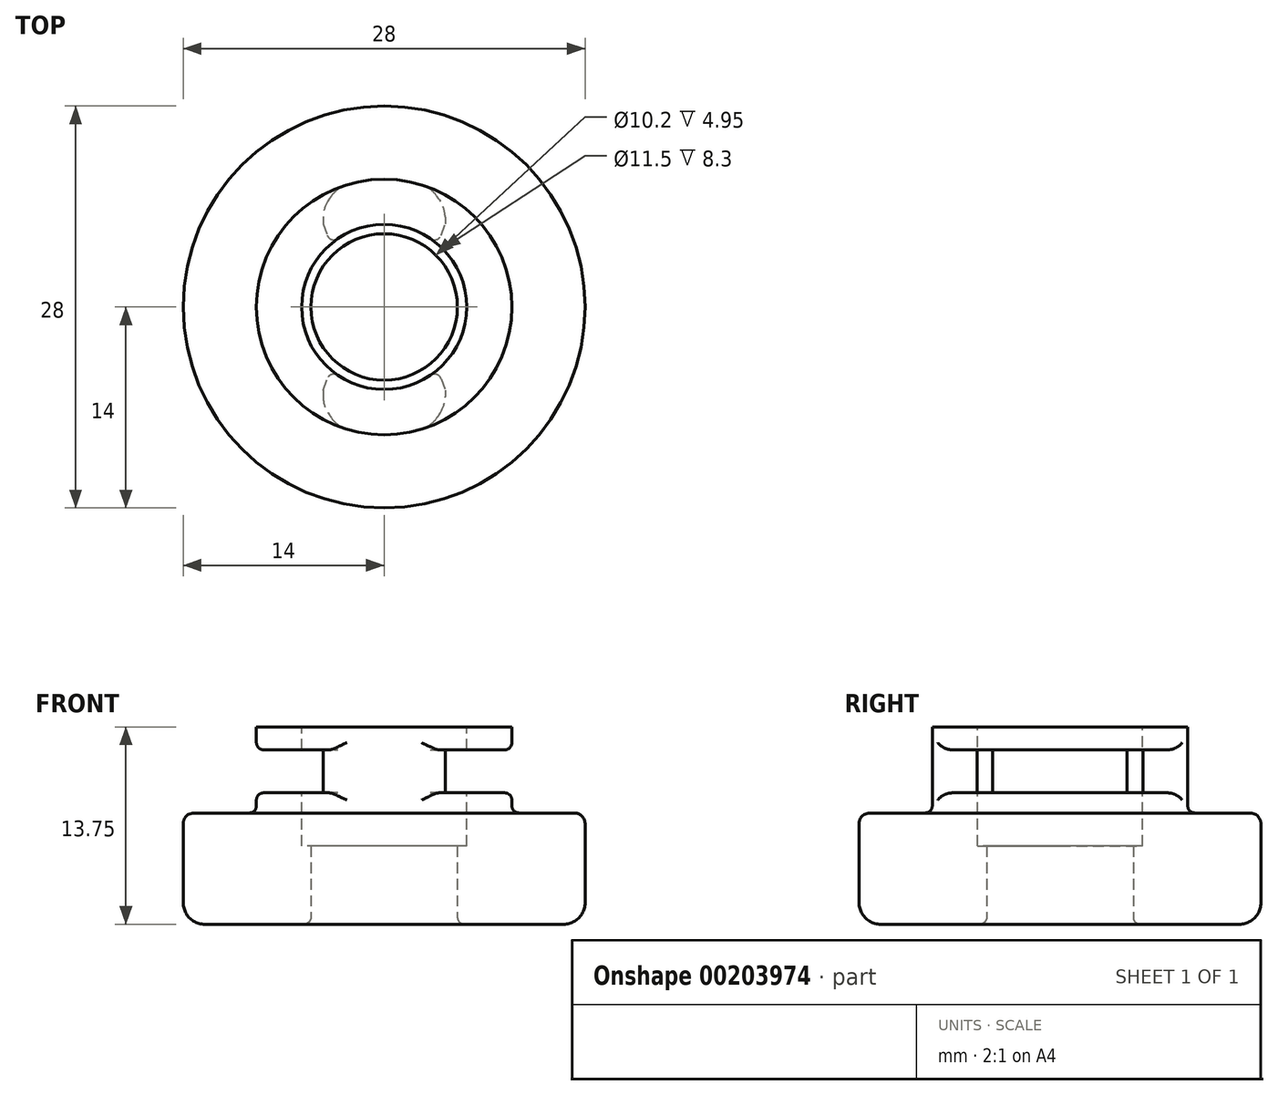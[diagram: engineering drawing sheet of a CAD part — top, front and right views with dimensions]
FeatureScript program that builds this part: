
annotation { "Feature Type Name" : "Feature", "Feature Type Description" : "" }
export const myFeature = defineFeature(function(context is Context, id is Id, definition is map)
    precondition{}
    {
        {
            var Q0;
            Q0=qCreatedBy(makeId("Top.planeOp"),FACE);
            var sketch = newSketch(context, id + "F0", { "sketchPlane" : qUnion([Q0])});
            skCircle(sketch, "E0", {"center": v(0, 0) * mm, "radius": 14 * mm});
            skCircle(sketch, "E1", {"center": v(0, 0) * mm, "radius": 5.1 * mm});
            skSolve(sketch);
        }
        {
            var Q0;
            Q0=makeQuery(id+"F0.imprint","IMPRINT",FACE,{"disambiguationData":[TD([[makeQuery(id+"F0.imprint","IMPRINT",EDGE,{"derivedFrom":sQuery(id+"F0.wireOp",EDGE,"E0")}),1.0]])]});
            extrude(context, id + "F1", {"entities" : qUnion([Q0]), "depth" : 13.75 * mm});
        }
        {
            var Q0;
            Q0=makeQuery(id+"F1.opExtrude","CAP_FACE",FACE,{"disambiguationData":[OSD([sQuery(id+"F0.wireOp",EDGE,"E0"),sQuery(id+"F0.wireOp",EDGE,"E1")])],"isStart":false});
            var sketch = newSketch(context, id + "F2", { "sketchPlane" : qUnion([Q0])});
            skCircle(sketch, "E2", {"center": v(0, 0) * mm, "radius": 8.9 * mm});
            skCircle(sketch, "E3", {"center": v(0, 0) * mm, "radius": 21.17 * mm});
            skSolve(sketch);
        }
        {
            var Q0;
            Q0=makeQuery(id+"F2.imprint","IMPRINT",FACE,{"disambiguationData":[TD([[makeQuery(id+"F2.imprint","IMPRINT",EDGE,{"derivedFrom":sQuery(id+"F2.wireOp",EDGE,"E3")}),1.0]])]});
            var Q1;
            Q1=makeQuery(id+"F2.imprint","IMPRINT",FACE,{"disambiguationData":[TD([[makeQuery(id+"F2.imprint","IMPRINT",EDGE,{"derivedFrom":sQuery(id+"F2.wireOp",EDGE,"E2")}),-1.0]])]});
            extrude(context, id + "F3", {"entities" : qUnion([Q0, Q1]), "operationType" : NewBodyOperationType.REMOVE, "oppositeDirection" : true, "depth" : 6 * mm});
        }
        {
            var Q0;
            Q0=qCreatedBy(makeId("Front.planeOp"),FACE);
            var sketch = newSketch(context, id + "F4", { "sketchPlane" : qUnion([Q0])});
            skLineSegment(sketch, "E4.bottom", {"start": v(-30.77, 12.15) * mm, "end": v(-4.25, 12.15) * mm});
            skLineSegment(sketch, "E4.top", {"start": v(-30.77, 9.15) * mm, "end": v(-4.25, 9.15) * mm});
            skLineSegment(sketch, "E4.left", {"start": v(-30.77, 12.15) * mm, "end": v(-30.77, 9.15) * mm});
            skLineSegment(sketch, "E4.right", {"start": v(-4.25, 12.15) * mm, "end": v(-4.25, 9.15) * mm});
            skLineSegment(sketch, "E5.bottom", {"start": v(4.25, 12.15) * mm, "end": v(38.35, 12.15) * mm});
            skLineSegment(sketch, "E5.top", {"start": v(4.25, 9.15) * mm, "end": v(38.35, 9.15) * mm});
            skLineSegment(sketch, "E5.left", {"start": v(4.25, 12.15) * mm, "end": v(4.25, 9.15) * mm});
            skLineSegment(sketch, "E5.right", {"start": v(38.35, 12.15) * mm, "end": v(38.35, 9.15) * mm});
            skSolve(sketch);
        }
        {
            var Q0;
            Q0=makeQuery(id+"F4.imprint","IMPRINT",FACE,{"disambiguationData":[TD([[makeQuery(id+"F4.imprint","IMPRINT",EDGE,{"derivedFrom":sQuery(id+"F4.wireOp",EDGE,"E4.bottom")}),-1.0]])]});
            var Q1;
            Q1=makeQuery(id+"F4.imprint","IMPRINT",FACE,{"disambiguationData":[TD([[makeQuery(id+"F4.imprint","IMPRINT",EDGE,{"derivedFrom":sQuery(id+"F4.wireOp",EDGE,"E5.bottom")}),-1.0]])]});
            extrude(context, id + "F5", {"entities" : qUnion([Q0, Q1]), "operationType" : NewBodyOperationType.REMOVE, "endBound" : BoundingType.SYMMETRIC, "oppositeDirection" : true, "depth" : 25 * mm});
        }
        {
            var Q0;
            Q0=makeQuery(id+"F1.opExtrude","CAP_FACE",FACE,{"disambiguationData":[OSD([sQuery(id+"F0.wireOp",EDGE,"E0"),sQuery(id+"F0.wireOp",EDGE,"E1")])],"isStart":false});
            var sketch = newSketch(context, id + "F6", { "sketchPlane" : qUnion([Q0])});
            skCircle(sketch, "E6", {"center": v(0, 0) * mm, "radius": 5.75 * mm});
            skSolve(sketch);
        }
        {
            var Q0;
            Q0=makeQuery(id+"F6.imprint","IMPRINT",FACE,{"disambiguationData":[TD([[makeQuery(id+"F6.imprint","IMPRINT",EDGE,{"derivedFrom":sQuery(id+"F6.wireOp",EDGE,"E6")}),1.0]])]});
            var Q1;
            Q1=makeQuery(id+"F6.imprint","IMPRINT",FACE,{"disambiguationData":[TD([[makeQuery(id+"F6.imprint","IMPRINT",EDGE,{"derivedFrom":makeQuery(id+"F1.opExtrude","CAP_EDGE",EDGE,{"disambiguationData":[OSD([sQuery(id+"F0.wireOp",EDGE,"E1")])],"isStart":false})}),1.0]])]});
            extrude(context, id + "F7", {"entities" : qUnion([Q0, Q1]), "operationType" : NewBodyOperationType.REMOVE, "oppositeDirection" : true, "depth" : 8.3 * mm});
        }
        {
            var Q0;
            Q0=makeQuery(id+"F1.opExtrude","CAP_EDGE",EDGE,{"disambiguationData":[OSD([sQuery(id+"F0.wireOp",EDGE,"E1")])],"isStart":true});
            fillet(context, id + "F8", {"entities" : qUnion([Q0]), "radius" : 0.5 * mm, "tangentPropagation" : true, "allowEdgeOverflow" : false});
        }
        {
            var Q0;
            Q0=makeQuery(id+"F1.opExtrude","CAP_EDGE",EDGE,{"disambiguationData":[OSD([sQuery(id+"F0.wireOp",EDGE,"E0")])],"isStart":true});
            fillet(context, id + "F9", {"entities" : qUnion([Q0]), "radius" : 1.5 * mm, "tangentPropagation" : true, "allowEdgeOverflow" : false});
        }
        {
            var Q0;
            Q0=makeQuery(id+"F3.boolean.opBoolean","INTERSECT",EDGE,{"derivedFrom":[makeQuery(id+"F1.opExtrude","SWEPT_FACE",FACE,{"disambiguationData":[OSD([sQuery(id+"F0.wireOp",EDGE,"E0")])]}),makeQuery(id+"F3.opExtrude","CAP_FACE",FACE,{"disambiguationData":[OSD([sQuery(id+"F2.wireOp",EDGE,"E2"),sQuery(id+"F2.wireOp",EDGE,"E3")])],"isStart":false})]});
            fillet(context, id + "F10", {"entities" : qUnion([Q0]), "radius" : 0.75 * mm, "tangentPropagation" : true, "allowEdgeOverflow" : false});
        }
        {
            var Q0;
            Q0=makeQuery(id+"F3.boolean.opBoolean","COPY",EDGE,{"derivedFrom":makeQuery(id+"F3.opExtrude","CAP_EDGE",EDGE,{"disambiguationData":[OSD([sQuery(id+"F2.wireOp",EDGE,"E2")])],"isStart":false})});
            var Q1;
            Q1=makeQuery(id+"F3.boolean.opBoolean","COPY",EDGE,{"derivedFrom":makeQuery(id+"F3.opExtrude","CAP_EDGE",EDGE,{"disambiguationData":[OSD([sQuery(id+"F2.wireOp",EDGE,"E2")])],"isStart":true})});
            var Q2;
            Q2=makeQuery(id+"F7.boolean.opBoolean","COPY",EDGE,{"derivedFrom":makeQuery(id+"F7.opExtrude","CAP_EDGE",EDGE,{"disambiguationData":[OSD([sQuery(id+"F6.wireOp",EDGE,"E6")])],"isStart":true})});
            fillet(context, id + "F11", {"entities" : qUnion([Q0, Q1, Q2]), "radius" : 0.5 * mm, "tangentPropagation" : true, "allowEdgeOverflow" : false});
        }
        {
            var Q0;
            Q0=makeQuery(id+"F5.boolean.opBoolean","INTERSECT",EDGE,{"disambiguationData":[OD(1.0)],"derivedFrom":[makeQuery(id+"F3.boolean.opBoolean","COPY",FACE,{"derivedFrom":makeQuery(id+"F3.opExtrude","SWEPT_FACE",FACE,{"disambiguationData":[OSD([sQuery(id+"F2.wireOp",EDGE,"E2")])]})}),makeQuery(id+"F5.opExtrude","SWEPT_FACE",FACE,{"disambiguationData":[OSD([sQuery(id+"F4.wireOp",EDGE,"E4.right")])]})]});
            var Q1;
            Q1=makeQuery(id+"F5.boolean.opBoolean","INTERSECT",EDGE,{"disambiguationData":[OD(0.0)],"derivedFrom":[makeQuery(id+"F3.boolean.opBoolean","COPY",FACE,{"derivedFrom":makeQuery(id+"F3.opExtrude","SWEPT_FACE",FACE,{"disambiguationData":[OSD([sQuery(id+"F2.wireOp",EDGE,"E2")])]})}),makeQuery(id+"F5.opExtrude","SWEPT_FACE",FACE,{"disambiguationData":[OSD([sQuery(id+"F4.wireOp",EDGE,"E4.right")])]})]});
            var Q2;
            Q2=makeQuery(id+"F5.boolean.opBoolean","INTERSECT",EDGE,{"disambiguationData":[OD(0.0)],"derivedFrom":[makeQuery(id+"F3.boolean.opBoolean","COPY",FACE,{"derivedFrom":makeQuery(id+"F3.opExtrude","SWEPT_FACE",FACE,{"disambiguationData":[OSD([sQuery(id+"F2.wireOp",EDGE,"E2")])]})}),makeQuery(id+"F5.opExtrude","SWEPT_FACE",FACE,{"disambiguationData":[OSD([sQuery(id+"F4.wireOp",EDGE,"E5.left")])]})]});
            var Q3;
            Q3=makeQuery(id+"F5.boolean.opBoolean","INTERSECT",EDGE,{"disambiguationData":[OD(1.0)],"derivedFrom":[makeQuery(id+"F3.boolean.opBoolean","COPY",FACE,{"derivedFrom":makeQuery(id+"F3.opExtrude","SWEPT_FACE",FACE,{"disambiguationData":[OSD([sQuery(id+"F2.wireOp",EDGE,"E2")])]})}),makeQuery(id+"F5.opExtrude","SWEPT_FACE",FACE,{"disambiguationData":[OSD([sQuery(id+"F4.wireOp",EDGE,"E5.left")])]})]});
            chamfer(context, id + "F12", {"entities" : qUnion([Q0, Q1, Q2, Q3]), "width" : 1.5 * mm, "tangentPropagation" : true});
        }
        {
            var Q0;
            {var subQ0=makeQuery(id+"F5.opExtrude","SWEPT_FACE",FACE,{"disambiguationData":[OSD([sQuery(id+"F4.wireOp",EDGE,"E4.right")])]});Q0=makeQuery(id+"F12.opChamfer","BLEND_EDGE",EDGE,{"blendedFrom":[makeQuery(id+"F5.boolean.opBoolean","INTERSECT",EDGE,{"disambiguationData":[OD(0.0)],"derivedFrom":[makeQuery(id+"F3.boolean.opBoolean","COPY",FACE,{"derivedFrom":makeQuery(id+"F3.opExtrude","SWEPT_FACE",FACE,{"disambiguationData":[OSD([sQuery(id+"F2.wireOp",EDGE,"E2")])]})}),subQ0]}),makeQuery(id+"F5.boolean.opBoolean","COPY",FACE,{"disambiguationData":[OD(0.0)],"derivedFrom":subQ0})],"blendedInto":[makeQuery(id+"F5.boolean.opBoolean","COPY",FACE,{"disambiguationData":[OD(0.0)],"derivedFrom":subQ0})]});}
            var Q1;
            {var subQ0=makeQuery(id+"F3.boolean.opBoolean","COPY",FACE,{"derivedFrom":makeQuery(id+"F3.opExtrude","SWEPT_FACE",FACE,{"disambiguationData":[OSD([sQuery(id+"F2.wireOp",EDGE,"E2")])]})});Q1=makeQuery(id+"F12.opChamfer","BLEND_EDGE",EDGE,{"blendedFrom":[makeQuery(id+"F5.boolean.opBoolean","INTERSECT",EDGE,{"disambiguationData":[OD(0.0)],"derivedFrom":[subQ0,makeQuery(id+"F5.opExtrude","SWEPT_FACE",FACE,{"disambiguationData":[OSD([sQuery(id+"F4.wireOp",EDGE,"E4.right")])]})]}),subQ0],"blendedInto":[subQ0]});}
            var Q2;
            {var subQ0=makeQuery(id+"F5.opExtrude","SWEPT_FACE",FACE,{"disambiguationData":[OSD([sQuery(id+"F4.wireOp",EDGE,"E4.right")])]});Q2=makeQuery(id+"F12.opChamfer","BLEND_EDGE",EDGE,{"blendedFrom":[makeQuery(id+"F5.boolean.opBoolean","INTERSECT",EDGE,{"disambiguationData":[OD(1.0)],"derivedFrom":[makeQuery(id+"F3.boolean.opBoolean","COPY",FACE,{"derivedFrom":makeQuery(id+"F3.opExtrude","SWEPT_FACE",FACE,{"disambiguationData":[OSD([sQuery(id+"F2.wireOp",EDGE,"E2")])]})}),subQ0]}),makeQuery(id+"F5.boolean.opBoolean","COPY",FACE,{"disambiguationData":[OD(1.0)],"derivedFrom":subQ0})],"blendedInto":[makeQuery(id+"F5.boolean.opBoolean","COPY",FACE,{"disambiguationData":[OD(1.0)],"derivedFrom":subQ0})]});}
            var Q3;
            {var subQ0=makeQuery(id+"F3.boolean.opBoolean","COPY",FACE,{"derivedFrom":makeQuery(id+"F3.opExtrude","SWEPT_FACE",FACE,{"disambiguationData":[OSD([sQuery(id+"F2.wireOp",EDGE,"E2")])]})});Q3=makeQuery(id+"F12.opChamfer","BLEND_EDGE",EDGE,{"blendedFrom":[makeQuery(id+"F5.boolean.opBoolean","INTERSECT",EDGE,{"disambiguationData":[OD(1.0)],"derivedFrom":[subQ0,makeQuery(id+"F5.opExtrude","SWEPT_FACE",FACE,{"disambiguationData":[OSD([sQuery(id+"F4.wireOp",EDGE,"E4.right")])]})]}),subQ0],"blendedInto":[subQ0]});}
            var Q4;
            {var subQ0=makeQuery(id+"F3.boolean.opBoolean","COPY",FACE,{"derivedFrom":makeQuery(id+"F3.opExtrude","SWEPT_FACE",FACE,{"disambiguationData":[OSD([sQuery(id+"F2.wireOp",EDGE,"E2")])]})});Q4=makeQuery(id+"F12.opChamfer","BLEND_EDGE",EDGE,{"blendedFrom":[makeQuery(id+"F5.boolean.opBoolean","INTERSECT",EDGE,{"disambiguationData":[OD(0.0)],"derivedFrom":[subQ0,makeQuery(id+"F5.opExtrude","SWEPT_FACE",FACE,{"disambiguationData":[OSD([sQuery(id+"F4.wireOp",EDGE,"E5.left")])]})]}),subQ0],"blendedInto":[subQ0]});}
            var Q5;
            {var subQ0=makeQuery(id+"F5.opExtrude","SWEPT_FACE",FACE,{"disambiguationData":[OSD([sQuery(id+"F4.wireOp",EDGE,"E5.left")])]});Q5=makeQuery(id+"F12.opChamfer","BLEND_EDGE",EDGE,{"blendedFrom":[makeQuery(id+"F5.boolean.opBoolean","INTERSECT",EDGE,{"disambiguationData":[OD(0.0)],"derivedFrom":[makeQuery(id+"F3.boolean.opBoolean","COPY",FACE,{"derivedFrom":makeQuery(id+"F3.opExtrude","SWEPT_FACE",FACE,{"disambiguationData":[OSD([sQuery(id+"F2.wireOp",EDGE,"E2")])]})}),subQ0]}),makeQuery(id+"F5.boolean.opBoolean","COPY",FACE,{"disambiguationData":[OD(0.0)],"derivedFrom":subQ0})],"blendedInto":[makeQuery(id+"F5.boolean.opBoolean","COPY",FACE,{"disambiguationData":[OD(0.0)],"derivedFrom":subQ0})]});}
            var Q6;
            {var subQ0=makeQuery(id+"F5.opExtrude","SWEPT_FACE",FACE,{"disambiguationData":[OSD([sQuery(id+"F4.wireOp",EDGE,"E5.left")])]});Q6=makeQuery(id+"F12.opChamfer","BLEND_EDGE",EDGE,{"blendedFrom":[makeQuery(id+"F5.boolean.opBoolean","INTERSECT",EDGE,{"disambiguationData":[OD(1.0)],"derivedFrom":[makeQuery(id+"F3.boolean.opBoolean","COPY",FACE,{"derivedFrom":makeQuery(id+"F3.opExtrude","SWEPT_FACE",FACE,{"disambiguationData":[OSD([sQuery(id+"F2.wireOp",EDGE,"E2")])]})}),subQ0]}),makeQuery(id+"F5.boolean.opBoolean","COPY",FACE,{"disambiguationData":[OD(1.0)],"derivedFrom":subQ0})],"blendedInto":[makeQuery(id+"F5.boolean.opBoolean","COPY",FACE,{"disambiguationData":[OD(1.0)],"derivedFrom":subQ0})]});}
            var Q7;
            {var subQ0=makeQuery(id+"F3.boolean.opBoolean","COPY",FACE,{"derivedFrom":makeQuery(id+"F3.opExtrude","SWEPT_FACE",FACE,{"disambiguationData":[OSD([sQuery(id+"F2.wireOp",EDGE,"E2")])]})});Q7=makeQuery(id+"F12.opChamfer","BLEND_EDGE",EDGE,{"blendedFrom":[makeQuery(id+"F5.boolean.opBoolean","INTERSECT",EDGE,{"disambiguationData":[OD(1.0)],"derivedFrom":[subQ0,makeQuery(id+"F5.opExtrude","SWEPT_FACE",FACE,{"disambiguationData":[OSD([sQuery(id+"F4.wireOp",EDGE,"E5.left")])]})]}),subQ0],"blendedInto":[subQ0]});}
            fillet(context, id + "F13", {"entities" : qUnion([Q0, Q1, Q2, Q3, Q4, Q5, Q6, Q7]), "radius" : 2 * mm, "tangentPropagation" : true, "allowEdgeOverflow" : false});
        }
        {
            var Q0;
            Q0=makeQuery(id+"F5.boolean.opBoolean","INTERSECT",EDGE,{"derivedFrom":[makeQuery(id+"F3.boolean.opBoolean","COPY",FACE,{"derivedFrom":makeQuery(id+"F3.opExtrude","SWEPT_FACE",FACE,{"disambiguationData":[OSD([sQuery(id+"F2.wireOp",EDGE,"E2")])]})}),makeQuery(id+"F5.opExtrude","SWEPT_FACE",FACE,{"disambiguationData":[OSD([sQuery(id+"F4.wireOp",EDGE,"E5.top")])]})]});
            var Q1;
            Q1=makeQuery(id+"F5.boolean.opBoolean","INTERSECT",EDGE,{"derivedFrom":[makeQuery(id+"F3.boolean.opBoolean","COPY",FACE,{"derivedFrom":makeQuery(id+"F3.opExtrude","SWEPT_FACE",FACE,{"disambiguationData":[OSD([sQuery(id+"F2.wireOp",EDGE,"E2")])]})}),makeQuery(id+"F5.opExtrude","SWEPT_FACE",FACE,{"disambiguationData":[OSD([sQuery(id+"F4.wireOp",EDGE,"E5.bottom")])]})]});
            var Q2;
            Q2=makeQuery(id+"F5.boolean.opBoolean","INTERSECT",EDGE,{"derivedFrom":[makeQuery(id+"F3.boolean.opBoolean","COPY",FACE,{"derivedFrom":makeQuery(id+"F3.opExtrude","SWEPT_FACE",FACE,{"disambiguationData":[OSD([sQuery(id+"F2.wireOp",EDGE,"E2")])]})}),makeQuery(id+"F5.opExtrude","SWEPT_FACE",FACE,{"disambiguationData":[OSD([sQuery(id+"F4.wireOp",EDGE,"E4.bottom")])]})]});
            var Q3;
            Q3=makeQuery(id+"F5.boolean.opBoolean","INTERSECT",EDGE,{"derivedFrom":[makeQuery(id+"F3.boolean.opBoolean","COPY",FACE,{"derivedFrom":makeQuery(id+"F3.opExtrude","SWEPT_FACE",FACE,{"disambiguationData":[OSD([sQuery(id+"F2.wireOp",EDGE,"E2")])]})}),makeQuery(id+"F5.opExtrude","SWEPT_FACE",FACE,{"disambiguationData":[OSD([sQuery(id+"F4.wireOp",EDGE,"E4.top")])]})]});
            fillet(context, id + "F14", {"entities" : qUnion([Q0, Q1, Q2, Q3]), "radius" : 0.5 * mm, "tangentPropagation" : true, "allowEdgeOverflow" : false});
        }
        {
            var Q0;
            Q0=makeQuery(id+"F7.boolean.opBoolean","INTERSECT",EDGE,{"derivedFrom":[makeQuery(id+"F5.boolean.opBoolean","COPY",FACE,{"disambiguationData":[OD(1.0)],"derivedFrom":makeQuery(id+"F5.opExtrude","SWEPT_FACE",FACE,{"disambiguationData":[OSD([sQuery(id+"F4.wireOp",EDGE,"E4.right")])]})}),makeQuery(id+"F7.opExtrude","SWEPT_FACE",FACE,{"disambiguationData":[OSD([sQuery(id+"F6.wireOp",EDGE,"E6")])]})]});
            var Q1;
            Q1=makeQuery(id+"F7.boolean.opBoolean","INTERSECT",EDGE,{"derivedFrom":[makeQuery(id+"F5.boolean.opBoolean","COPY",FACE,{"disambiguationData":[OD(0.0)],"derivedFrom":makeQuery(id+"F5.opExtrude","SWEPT_FACE",FACE,{"disambiguationData":[OSD([sQuery(id+"F4.wireOp",EDGE,"E4.right")])]})}),makeQuery(id+"F7.opExtrude","SWEPT_FACE",FACE,{"disambiguationData":[OSD([sQuery(id+"F6.wireOp",EDGE,"E6")])]})]});
            var Q2;
            Q2=makeQuery(id+"F7.boolean.opBoolean","INTERSECT",EDGE,{"derivedFrom":[makeQuery(id+"F5.boolean.opBoolean","COPY",FACE,{"disambiguationData":[OD(0.0)],"derivedFrom":makeQuery(id+"F5.opExtrude","SWEPT_FACE",FACE,{"disambiguationData":[OSD([sQuery(id+"F4.wireOp",EDGE,"E5.left")])]})}),makeQuery(id+"F7.opExtrude","SWEPT_FACE",FACE,{"disambiguationData":[OSD([sQuery(id+"F6.wireOp",EDGE,"E6")])]})]});
            var Q3;
            Q3=makeQuery(id+"F7.boolean.opBoolean","INTERSECT",EDGE,{"derivedFrom":[makeQuery(id+"F5.boolean.opBoolean","COPY",FACE,{"disambiguationData":[OD(1.0)],"derivedFrom":makeQuery(id+"F5.opExtrude","SWEPT_FACE",FACE,{"disambiguationData":[OSD([sQuery(id+"F4.wireOp",EDGE,"E5.left")])]})}),makeQuery(id+"F7.opExtrude","SWEPT_FACE",FACE,{"disambiguationData":[OSD([sQuery(id+"F6.wireOp",EDGE,"E6")])]})]});
            chamfer(context, id + "F15", {"entities" : qUnion([Q0, Q1, Q2, Q3]), "chamferType" : ChamferType.TWO_OFFSETS, "width1" : 1 * mm, "oppositeDirection" : false, "width2" : 2 * mm, "tangentPropagation" : true});
        }
        {
            var Q0;
            {var subQ0=makeQuery(id+"F7.opExtrude","SWEPT_FACE",FACE,{"disambiguationData":[OSD([sQuery(id+"F6.wireOp",EDGE,"E6")])]});Q0=makeQuery(id+"F15.opChamfer","BLEND_EDGE",EDGE,{"blendedFrom":[makeQuery(id+"F7.boolean.opBoolean","INTERSECT",EDGE,{"derivedFrom":[makeQuery(id+"F5.boolean.opBoolean","COPY",FACE,{"disambiguationData":[OD(0.0)],"derivedFrom":makeQuery(id+"F5.opExtrude","SWEPT_FACE",FACE,{"disambiguationData":[OSD([sQuery(id+"F4.wireOp",EDGE,"E5.left")])]})}),subQ0]}),makeQuery(id+"F7.boolean.opBoolean","COPY",FACE,{"derivedFrom":subQ0})],"blendedInto":[makeQuery(id+"F7.boolean.opBoolean","COPY",FACE,{"derivedFrom":subQ0})]});}
            var Q1;
            {var subQ0=makeQuery(id+"F7.opExtrude","SWEPT_FACE",FACE,{"disambiguationData":[OSD([sQuery(id+"F6.wireOp",EDGE,"E6")])]});Q1=makeQuery(id+"F15.opChamfer","BLEND_EDGE",EDGE,{"blendedFrom":[makeQuery(id+"F7.boolean.opBoolean","INTERSECT",EDGE,{"derivedFrom":[makeQuery(id+"F5.boolean.opBoolean","COPY",FACE,{"disambiguationData":[OD(0.0)],"derivedFrom":makeQuery(id+"F5.opExtrude","SWEPT_FACE",FACE,{"disambiguationData":[OSD([sQuery(id+"F4.wireOp",EDGE,"E4.right")])]})}),subQ0]}),makeQuery(id+"F7.boolean.opBoolean","COPY",FACE,{"derivedFrom":subQ0})],"blendedInto":[makeQuery(id+"F7.boolean.opBoolean","COPY",FACE,{"derivedFrom":subQ0})]});}
            var Q2;
            {var subQ0=makeQuery(id+"F7.opExtrude","SWEPT_FACE",FACE,{"disambiguationData":[OSD([sQuery(id+"F6.wireOp",EDGE,"E6")])]});Q2=makeQuery(id+"F15.opChamfer","BLEND_EDGE",EDGE,{"blendedFrom":[makeQuery(id+"F7.boolean.opBoolean","INTERSECT",EDGE,{"derivedFrom":[makeQuery(id+"F5.boolean.opBoolean","COPY",FACE,{"disambiguationData":[OD(1.0)],"derivedFrom":makeQuery(id+"F5.opExtrude","SWEPT_FACE",FACE,{"disambiguationData":[OSD([sQuery(id+"F4.wireOp",EDGE,"E4.right")])]})}),subQ0]}),makeQuery(id+"F7.boolean.opBoolean","COPY",FACE,{"derivedFrom":subQ0})],"blendedInto":[makeQuery(id+"F7.boolean.opBoolean","COPY",FACE,{"derivedFrom":subQ0})]});}
            var Q3;
            {var subQ0=makeQuery(id+"F7.opExtrude","SWEPT_FACE",FACE,{"disambiguationData":[OSD([sQuery(id+"F6.wireOp",EDGE,"E6")])]});Q3=makeQuery(id+"F15.opChamfer","BLEND_EDGE",EDGE,{"blendedFrom":[makeQuery(id+"F7.boolean.opBoolean","INTERSECT",EDGE,{"derivedFrom":[makeQuery(id+"F5.boolean.opBoolean","COPY",FACE,{"disambiguationData":[OD(1.0)],"derivedFrom":makeQuery(id+"F5.opExtrude","SWEPT_FACE",FACE,{"disambiguationData":[OSD([sQuery(id+"F4.wireOp",EDGE,"E5.left")])]})}),subQ0]}),makeQuery(id+"F7.boolean.opBoolean","COPY",FACE,{"derivedFrom":subQ0})],"blendedInto":[makeQuery(id+"F7.boolean.opBoolean","COPY",FACE,{"derivedFrom":subQ0})]});}
            fillet(context, id + "F16", {"entities" : qUnion([Q0, Q1, Q2, Q3]), "radius" : 0.5 * mm, "tangentPropagation" : true, "allowEdgeOverflow" : false});
        }
    });
